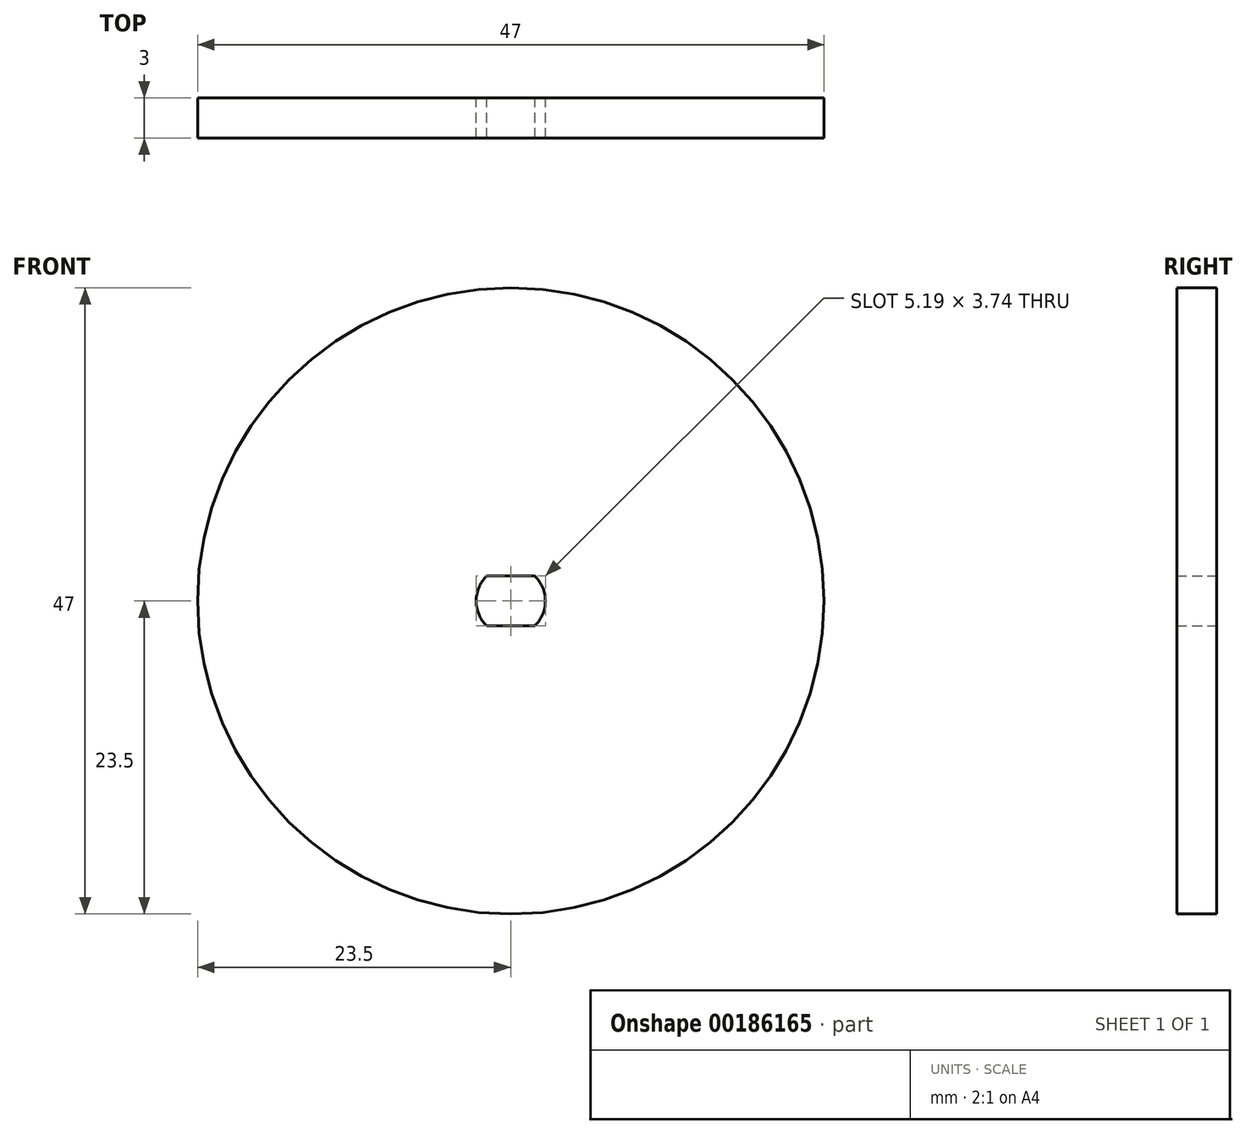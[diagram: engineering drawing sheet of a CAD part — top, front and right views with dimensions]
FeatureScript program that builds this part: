
annotation { "Feature Type Name" : "Feature", "Feature Type Description" : "" }
export const myFeature = defineFeature(function(context is Context, id is Id, definition is map)
    precondition{}
    {
        {
            var Q0;
            Q0=qCreatedBy(makeId("Front.planeOp"),FACE);
            var sketch = newSketch(context, id + "F0", { "sketchPlane" : qUnion([Q0])});
            skCircle(sketch, "E0", {"center": v(0, 0) * mm, "radius": 23.5 * mm});
            skCircle(sketch, "E1", {"center": v(0, 0) * mm, "radius": 2.6 * mm});
            skLineSegment(sketch, "E2", {"start": v(-1.8, 1.87) * mm, "end": v(1.8, 1.87) * mm});
            skLineSegment(sketch, "E3", {"start": v(1.8, -1.87) * mm, "end": v(-1.8, -1.87) * mm});
            skSolve(sketch);
        }
        {
            var Q0;
            {var subQ0=sQuery(id+"F0.wireOp",EDGE,"E2");Q0=makeQuery(id+"F0.imprint","IMPRINT",FACE,{"disambiguationData":[TD([[makeQuery(id+"F0.imprint","IMPRINT",EDGE,{"derivedFrom":subQ0}),1.0]])]});}
            var Q1;
            {var subQ0=sQuery(id+"F0.wireOp",EDGE,"E3");Q1=makeQuery(id+"F0.imprint","IMPRINT",FACE,{"disambiguationData":[TD([[makeQuery(id+"F0.imprint","IMPRINT",EDGE,{"derivedFrom":subQ0}),1.0]])]});}
            var Q2;
            Q2=makeQuery(id+"F0.imprint","IMPRINT",FACE,{"disambiguationData":[TD([[makeQuery(id+"F0.imprint","IMPRINT",EDGE,{"derivedFrom":sQuery(id+"F0.wireOp",EDGE,"E0")}),1.0]])]});
            extrude(context, id + "F1", {"entities" : qUnion([Q0, Q1, Q2]), "depth" : 3 * mm});
        }
    });
